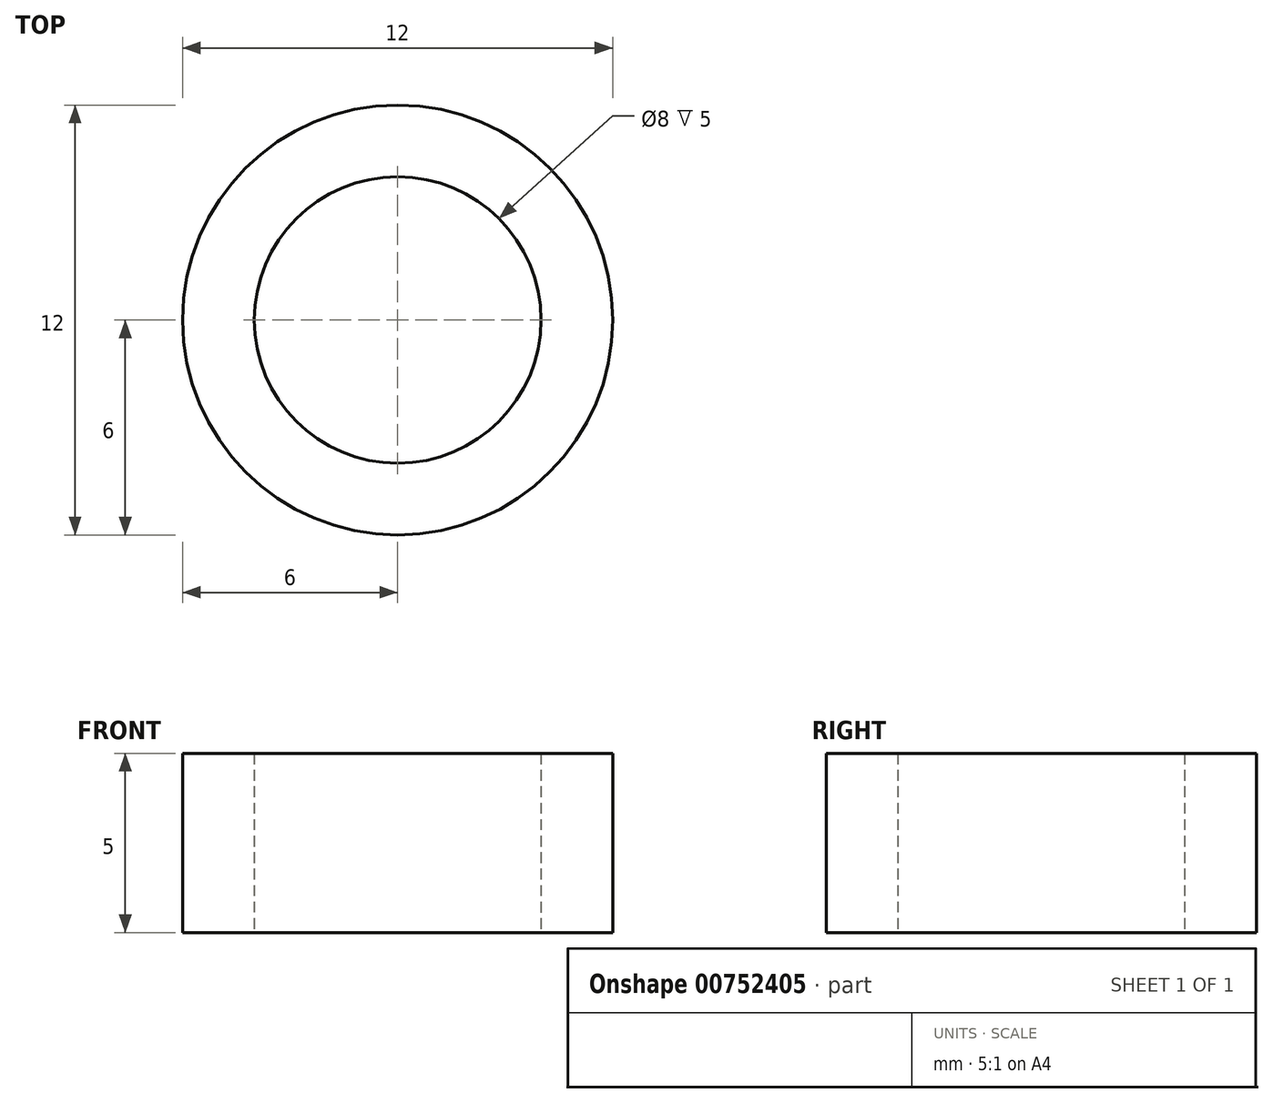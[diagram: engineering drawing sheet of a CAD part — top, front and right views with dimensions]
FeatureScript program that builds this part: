
annotation { "Feature Type Name" : "Feature", "Feature Type Description" : "" }
export const myFeature = defineFeature(function(context is Context, id is Id, definition is map)
    precondition{}
    {
        {
            var Q0;
            Q0=qCreatedBy(makeId("Top.planeOp"),FACE);
            var sketch = newSketch(context, id + "F0", { "sketchPlane" : qUnion([Q0])});
            skCircle(sketch, "E0", {"center": v(0, 0) * mm, "radius": 6 * mm});
            skCircle(sketch, "E1", {"center": v(0, 0) * mm, "radius": 4 * mm});
            skSolve(sketch);
        }
        {
            var Q0;
            Q0 = qSketchRegion(id + "F0", true);
            extrude(context, id + "F1", {"entities" : qUnion([Q0]), "depth" : 5 * mm, "offsetDistance" : 25 * mm});
        }
    });
